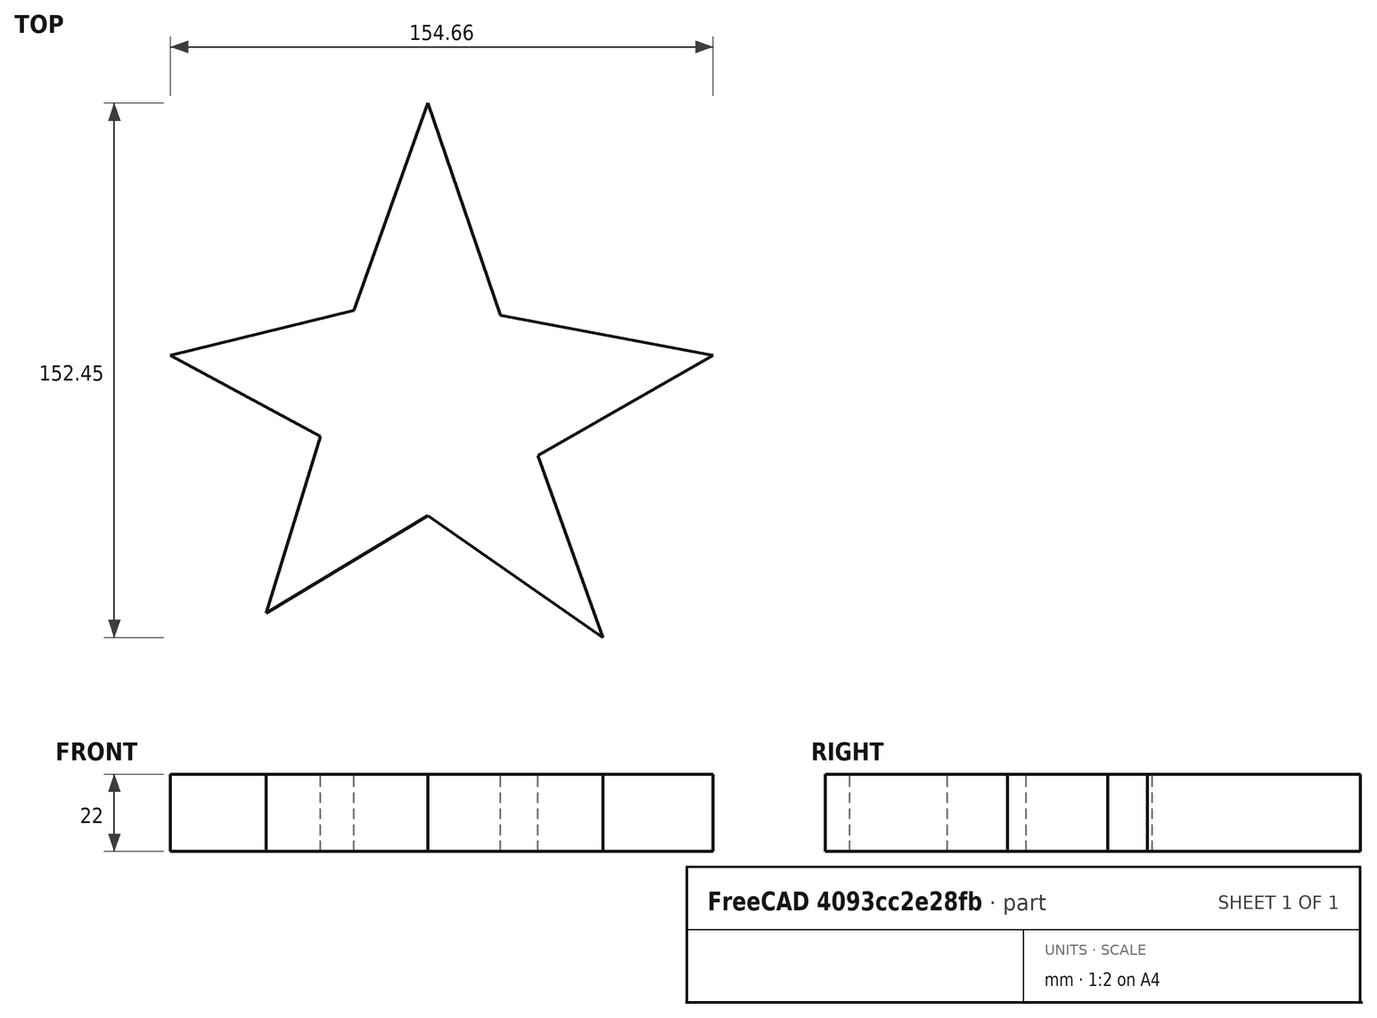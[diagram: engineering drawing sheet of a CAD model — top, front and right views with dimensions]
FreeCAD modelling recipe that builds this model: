
FCSTD DOCUMENT  (FreeCAD 1.0R39319 (Git))
Label: ojt16p01_sketchstar
License: All rights reserved
LicenseURL: https://en.wikipedia.org/wiki/All_rights_reserved
objects: Sketcher::SketchObject×2, PartDesign::Pad×1, PartDesign::Body×1
note: 8 computed .brp shape members not serialized (recipe doc carries the construction recipe); baked Part::Feature solids carry a one-line shape summary decoded from their .brp

FEATURE [Sketcher::SketchObject] Sketch
  ArcFitTolerance = 1e-06
  AttachmentSupport = -> [XY_Plane]
  FullyConstrained = true
  MakeInternals = false
  MapMode = 5
FEATURE [Sketcher::SketchObject] Sketch001
  ArcFitTolerance = 1e-06
  AttachmentSupport = -> [XY_Plane]
  FullyConstrained = false
  MakeInternals = false
  MapMode = 5
  sketch-geometry (10):
    g0: LineSegment StartX=0 StartY=72.0081 StartZ=0 EndX=20.71 EndY=11.3987 EndZ=0
    g1: LineSegment StartX=20.71 StartY=11.3987 StartZ=0 EndX=81.3091 EndY=0 EndZ=0
    g2: LineSegment StartX=81.3091 StartY=0 StartZ=0 EndX=31.4335 EndY=-28.5814 EndZ=0
    g3: LineSegment StartX=31.4335 StartY=-28.5814 StartZ=0 EndX=49.9323 EndY=-80.4426 EndZ=0
    g4: LineSegment StartX=49.9323 StartY=-80.4426 StartZ=0 EndX=0 EndY=-45.6543 EndZ=0
    g5: LineSegment StartX=0 StartY=-45.6543 StartZ=0 EndX=-46.0837 EndY=-73.485 EndZ=0
    g6: LineSegment StartX=-46.0837 StartY=-73.485 StartZ=0 EndX=-30.5966 EndY=-23.1328 EndZ=0
    g7: LineSegment StartX=-30.5966 StartY=-23.1328 StartZ=0 EndX=-73.3472 EndY=0 EndZ=0
    g8: LineSegment StartX=-73.3472 StartY=0 StartZ=0 EndX=-21.0361 EndY=12.7903 EndZ=0
    g9: LineSegment StartX=-21.0361 StartY=12.7903 StartZ=0 EndX=0 EndY=72.0081 EndZ=0
  constraints (14):
    c: PointOnObject(g0,g-2)
    c: Coincident(g0,g1)
    c: PointOnObject(g1,g-1)
    c: Coincident(g1,g2)
    c: Coincident(g2,g3)
    c: Coincident(g3,g4)
    c: PointOnObject(g4,g-2)
    c: Coincident(g4,g5)
    c: Coincident(g5,g6)
    c: Coincident(g6,g7)
    c: PointOnObject(g7,g-1)
    c: Coincident(g7,g8)
    c: Coincident(g8,g9)
    c: Coincident(g9,g0)
FEATURE [PartDesign::Pad] Pad
  Direction = (0,0,1)
  Length = 22
  Length2 = 10
  Profile = -> Sketch001
  ReferenceAxis = -> Sketch001 [N_Axis]
  Refine = true
  Suppressed = false
  Type = 0
FEATURE [PartDesign::Body] Body
  AllowCompound = false
  Group = -> [Sketch,Sketch001,Pad]
  Origin = -> Origin
  Tip = -> Pad
